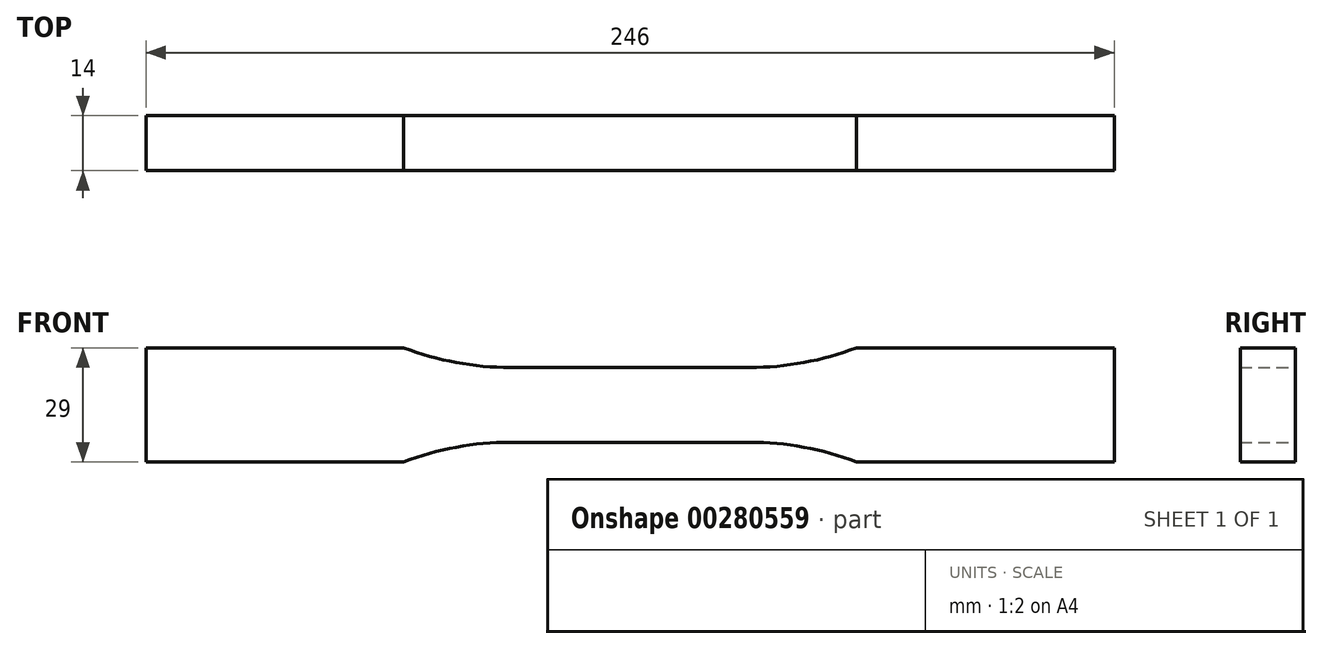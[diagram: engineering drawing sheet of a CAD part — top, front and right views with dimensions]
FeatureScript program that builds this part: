
annotation { "Feature Type Name" : "Feature", "Feature Type Description" : "" }
export const myFeature = defineFeature(function(context is Context, id is Id, definition is map)
    precondition{}
    {
        {
            var Q0;
            Q0=qCreatedBy(makeId("Front.planeOp"),FACE);
            var sketch = newSketch(context, id + "F0", { "sketchPlane" : qUnion([Q0])});
            skLineSegment(sketch, "E0", {"start": v(0, 9.5) * mm, "end": v(30.39, 9.5) * mm});
            skArc(sketch, "E1", {"start": v(30.39, 9.5) * mm, "mid": v(44.17, 10.76) * mm, "end": v(57.5, 14.5) * mm});
            skLineSegment(sketch, "E2", {"start": v(57.5, 14.5) * mm, "end": v(123, 14.5) * mm});
            skLineSegment(sketch, "E3", {"start": v(123, 14.5) * mm, "end": v(123, 0) * mm});
            skLineSegment(sketch, "E4.MirrorCS", {"start": v(57.5, -14.5) * mm, "end": v(123, -14.5) * mm});
            skArc(sketch, "E5.MirrorCS", {"start": v(30.39, -9.5) * mm, "mid": v(44.17, -10.76) * mm, "end": v(57.5, -14.5) * mm});
            skLineSegment(sketch, "E6.MirrorCS", {"start": v(123, -14.5) * mm, "end": v(123, 0) * mm});
            skLineSegment(sketch, "E7.MirrorCS", {"start": v(0, -9.5) * mm, "end": v(30.39, -9.5) * mm});
            skLineSegment(sketch, "E8.MirrorCS", {"start": v(0, -9.5) * mm, "end": v(-30.39, -9.5) * mm});
            skLineSegment(sketch, "E9.MirrorCS", {"start": v(-123, -14.5) * mm, "end": v(-123, 0) * mm});
            skLineSegment(sketch, "E10.MirrorCS", {"start": v(-57.5, -14.5) * mm, "end": v(-123, -14.5) * mm});
            skArc(sketch, "E11.MirrorCS", {"start": v(-30.39, 9.5) * mm, "mid": v(-44.17, 10.76) * mm, "end": v(-57.5, 14.5) * mm});
            skLineSegment(sketch, "E12.MirrorCS", {"start": v(0, 9.5) * mm, "end": v(-30.39, 9.5) * mm});
            skLineSegment(sketch, "E13.MirrorCS", {"start": v(-123, 14.5) * mm, "end": v(-123, 0) * mm});
            skLineSegment(sketch, "E14.MirrorCS", {"start": v(-57.5, 14.5) * mm, "end": v(-123, 14.5) * mm});
            skArc(sketch, "E15.MirrorCS", {"start": v(-30.39, -9.5) * mm, "mid": v(-44.17, -10.76) * mm, "end": v(-57.5, -14.5) * mm});
            skSolve(sketch);
        }
        {
            var Q0;
            Q0 = qSketchRegion(id + "F0", true);
            extrude(context, id + "F1", {"entities" : qUnion([Q0]), "endBound" : BoundingType.SYMMETRIC, "depth" : 14 * mm});
        }
    });
